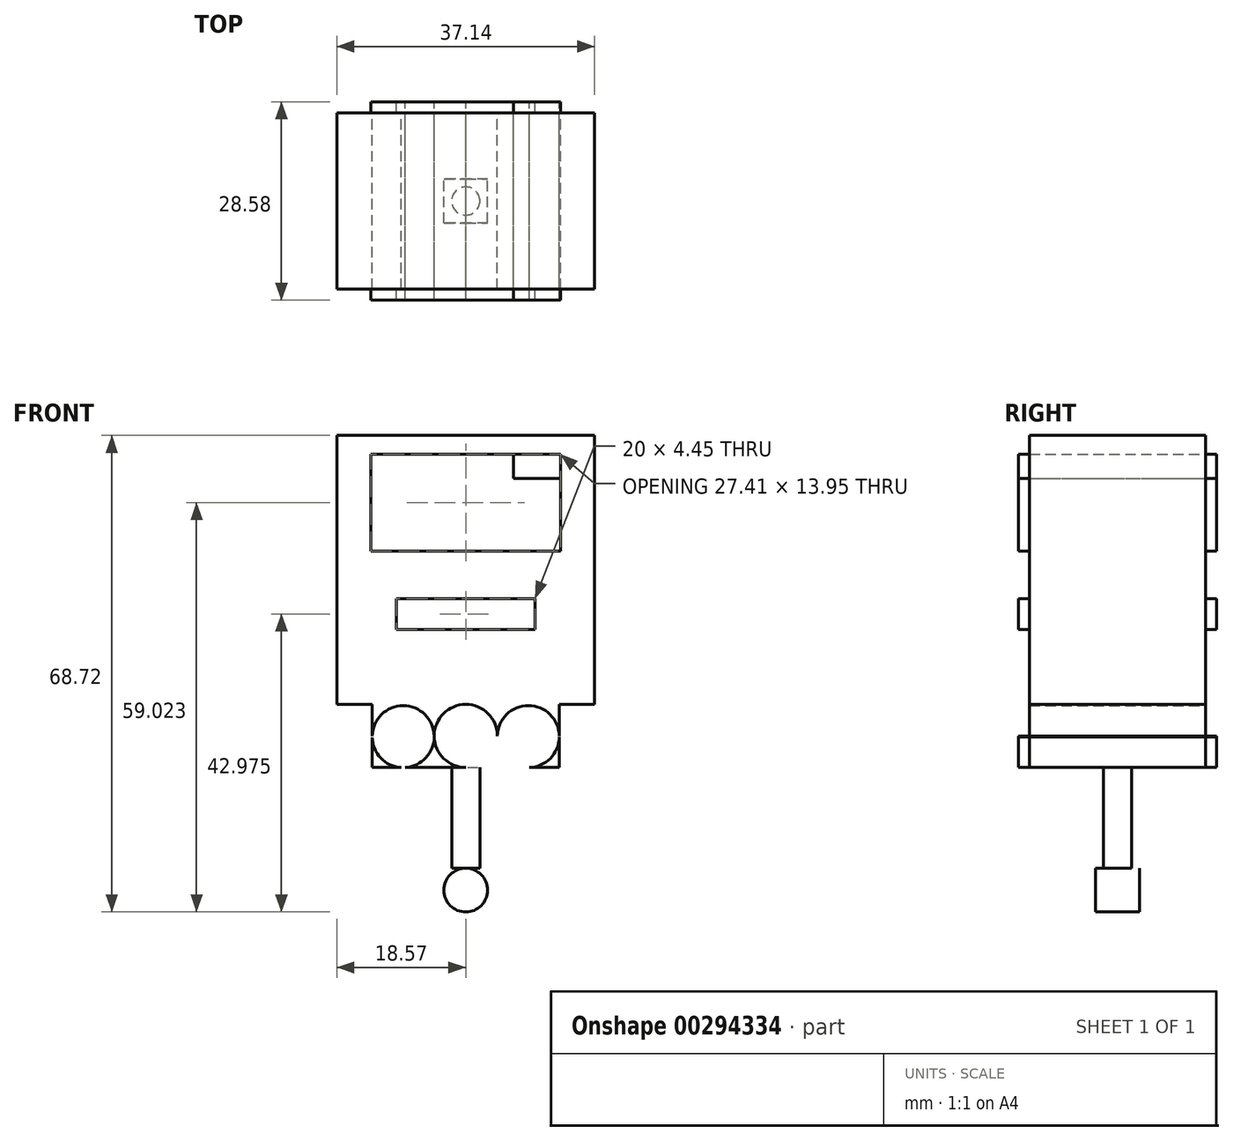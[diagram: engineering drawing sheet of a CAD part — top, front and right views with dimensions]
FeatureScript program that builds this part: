
annotation { "Feature Type Name" : "Feature", "Feature Type Description" : "" }
export const myFeature = defineFeature(function(context is Context, id is Id, definition is map)
    precondition{}
    {
        {
            var Q0;
            Q0=qCreatedBy(makeId("Front.planeOp"),FACE);
            var sketch = newSketch(context, id + "F0", { "sketchPlane" : qUnion([Q0])});
            skLineSegment(sketch, "E0.top", {"start": v(-13.49, -4.55) * mm, "end": v(13.49, -4.55) * mm});
            skLineSegment(sketch, "E0.left", {"start": v(-13.49, 4.55) * mm, "end": v(-13.49, -4.55) * mm});
            skLineSegment(sketch, "E0.right", {"start": v(13.49, 4.55) * mm, "end": v(13.49, -4.55) * mm});
            skPoint(sketch, "E0.middle", {"position": v(0, 0) * mm});
            skLineSegment(sketch, "E1", {"start": v(-13.49, 4.55) * mm, "end": v(-18.57, 4.55) * mm});
            skLineSegment(sketch, "E2", {"start": v(13.49, 4.55) * mm, "end": v(18.57, 4.55) * mm});
            skLineSegment(sketch, "E3.top", {"start": v(-18.57, 43.34) * mm, "end": v(18.57, 43.34) * mm});
            skLineSegment(sketch, "E3.left", {"start": v(-18.57, 4.55) * mm, "end": v(-18.57, 43.34) * mm});
            skLineSegment(sketch, "E3.right", {"start": v(18.57, 4.55) * mm, "end": v(18.57, 43.34) * mm});
            skPoint(sketch, "E4.endSnap0", {"position": v(0, -4.55) * mm});
            skLineSegment(sketch, "E5.bottom", {"start": v(-2.04, -4.55) * mm, "end": v(2.04, -4.55) * mm});
            skLineSegment(sketch, "E5.right", {"start": v(2.04, -4.55) * mm, "end": v(2.04, -19.08) * mm});
            skPoint(sketch, "E5.middle", {"position": v(0, -11.82) * mm});
            skCircle(sketch, "E6", {"center": v(0, 0) * mm, "radius": 4.55 * mm});
            skCircle(sketch, "E7", {"center": v(9.02, -0.09) * mm, "radius": 4.47 * mm});
            skPoint(sketch, "E7.second.point", {"position": v(4.55, 0) * mm});
            skPoint(sketch, "E7.third.point", {"position": v(8.9, -4.55) * mm});
            skCircle(sketch, "E8", {"center": v(-9.02, -0.1) * mm, "radius": 4.47 * mm});
            skPoint(sketch, "E8.second.point", {"position": v(-4.55, 0) * mm});
            skPoint(sketch, "E8.third.point", {"position": v(-8.7, -4.55) * mm});
            skLineSegment(sketch, "E9.bottom", {"start": v(-13.7, 26.67) * mm, "end": v(13.7, 26.67) * mm});
            skLineSegment(sketch, "E9.top", {"start": v(-13.7, 40.62) * mm, "end": v(13.7, 40.62) * mm});
            skLineSegment(sketch, "E9.left", {"start": v(-13.7, 26.67) * mm, "end": v(-13.7, 40.62) * mm});
            skLineSegment(sketch, "E9.right", {"start": v(13.7, 26.67) * mm, "end": v(13.7, 40.62) * mm});
            skPoint(sketch, "E9.middle", {"position": v(0, 33.64) * mm});
            skLineSegment(sketch, "E10.bottom", {"start": v(-10, 19.82) * mm, "end": v(10, 19.82) * mm});
            skLineSegment(sketch, "E10.top", {"start": v(-10, 15.37) * mm, "end": v(10, 15.37) * mm});
            skLineSegment(sketch, "E10.left", {"start": v(-10, 19.82) * mm, "end": v(-10, 15.37) * mm});
            skLineSegment(sketch, "E10.right", {"start": v(10, 19.82) * mm, "end": v(10, 15.37) * mm});
            skPoint(sketch, "E10.middle", {"position": v(0, 17.6) * mm});
            skLineSegment(sketch, "E11", {"start": v(0, 33.64) * mm, "end": v(0, 26.67) * mm});
            skLineSegment(sketch, "E12", {"start": v(0, 26.67) * mm, "end": v(0, 33.64) * mm});
            skLineSegment(sketch, "E13", {"start": v(0, 33.64) * mm, "end": v(0, 40.62) * mm});
            skLineSegment(sketch, "E14", {"start": v(0, 33.64) * mm, "end": v(13.7, 33.64) * mm});
            skLineSegment(sketch, "E15", {"start": v(13.7, 33.64) * mm, "end": v(-13.7, 33.64) * mm});
            skLineSegment(sketch, "E16", {"start": v(-13.7, 33.64) * mm, "end": v(-13.7, 26.67) * mm});
            skLineSegment(sketch, "E17", {"start": v(-13.7, 30.16) * mm, "end": v(13.7, 30.16) * mm});
            skLineSegment(sketch, "E18", {"start": v(13.7, 40.62) * mm, "end": v(13.7, 33.64) * mm});
            skLineSegment(sketch, "E19", {"start": v(13.7, 37.13) * mm, "end": v(-13.7, 37.13) * mm});
            skLineSegment(sketch, "E20", {"start": v(-13.7, 40.62) * mm, "end": v(0, 40.62) * mm});
            skLineSegment(sketch, "E21", {"start": v(-6.85, 40.62) * mm, "end": v(-6.85, 26.67) * mm});
            skLineSegment(sketch, "E22", {"start": v(0, 40.62) * mm, "end": v(13.7, 40.62) * mm});
            skLineSegment(sketch, "E23", {"start": v(6.85, 40.62) * mm, "end": v(6.85, 26.67) * mm});
            skLineSegment(sketch, "E24", {"start": v(0, 19.82) * mm, "end": v(0, 15.37) * mm});
            skLineSegment(sketch, "E25", {"start": v(-10, 19.82) * mm, "end": v(0, 19.82) * mm});
            skLineSegment(sketch, "E26", {"start": v(-5, 19.82) * mm, "end": v(-5, 15.37) * mm});
            skLineSegment(sketch, "E27", {"start": v(-5, 15.37) * mm, "end": v(10, 15.37) * mm});
            skLineSegment(sketch, "E28", {"start": v(0, 19.82) * mm, "end": v(10, 19.82) * mm});
            skLineSegment(sketch, "E29", {"start": v(5, 19.82) * mm, "end": v(5, 15.37) * mm});
            skCircle(sketch, "E30", {"center": v(0, -22.23) * mm, "radius": 3.15 * mm});
            skLineSegment(sketch, "E31", {"start": v(0, -36.46) * mm, "end": v(0, -30.92) * mm});
            skLineSegment(sketch, "E32", {"start": v(0, -30.92) * mm, "end": v(0, -43.93) * mm});
            skLineSegment(sketch, "E33", {"start": v(0, -19.08) * mm, "end": v(0, -4.55) * mm});
            skLineSegment(sketch, "E34", {"start": v(2.04, -19.08) * mm, "end": v(0, -19.08) * mm});
            skSolve(sketch);
        }
        {
            var Q0;
            {var subQ7=sQuery(id+"F0.wireOp",EDGE,"E1");Q0=makeQuery(id+"F0.imprint","IMPRINT",FACE,{"disambiguationData":[TD([[makeQuery(id+"F0.imprint","IMPRINT",EDGE,{"derivedFrom":subQ7}),-1.0]])]});}
            var Q1;
            {var subQ0=sQuery(id+"F0.wireOp",EDGE,"E0.left");var subQ1=sQuery(id+"F0.wireOp",EDGE,"E0.top");var subQ2=makeQuery(id+"F0.imprint","INTERSECT",VERTEX,{"derivedFrom":[subQ1,subQ0]});Q1=makeQuery(id+"F0.imprint","IMPRINT",FACE,{"disambiguationData":[TD([[makeQuery(id+"F0.imprint","IMPRINT",EDGE,{"disambiguationData":[TD([[subQ2,-1.0]])],"derivedFrom":subQ1}),1.0]])]});}
            var Q2;
            {var subQ3=sQuery(id+"F0.wireOp",EDGE,"E8");var subQ5=sQuery(id+"F0.wireOp",EDGE,"E6");var subQ7=makeQuery(id+"F0.imprint","INTERSECT",VERTEX,{"disambiguationData":[OD(1.0)],"derivedFrom":[subQ5,subQ3]});Q2=makeQuery(id+"F0.imprint","IMPRINT",FACE,{"disambiguationData":[TD([[makeQuery(id+"F0.imprint","IMPRINT",EDGE,{"disambiguationData":[TD([[subQ7,-1.0]])],"derivedFrom":subQ5}),-1.0]])]});}
            var Q3;
            {var subQ0=sQuery(id+"F0.wireOp",EDGE,"E5.bottom");var subQ5=sQuery(id+"F0.wireOp",EDGE,"E6");var subQ6=makeQuery(id+"F0.imprint","INTERSECT",VERTEX,{"derivedFrom":[subQ0,subQ5]});Q3=makeQuery(id+"F0.imprint","IMPRINT",FACE,{"disambiguationData":[TD([[makeQuery(id+"F0.imprint","IMPRINT",EDGE,{"disambiguationData":[TD([[subQ6,-1.0]])],"derivedFrom":subQ5}),-1.0]])]});}
            var Q4;
            {var subQ0=sQuery(id+"F0.wireOp",EDGE,"E0.right");var subQ1=sQuery(id+"F0.wireOp",EDGE,"E0.top");var subQ2=makeQuery(id+"F0.imprint","INTERSECT",VERTEX,{"derivedFrom":[subQ1,subQ0]});Q4=makeQuery(id+"F0.imprint","IMPRINT",FACE,{"disambiguationData":[TD([[makeQuery(id+"F0.imprint","IMPRINT",EDGE,{"disambiguationData":[TD([[subQ2,1.0]])],"derivedFrom":subQ1}),1.0]])]});}
            extrude(context, id + "F1", {"entities" : qUnion([Q0, Q1, Q2, Q3, Q4]), "endBound" : BoundingType.SYMMETRIC, "depth" : 25.4 * mm});
        }
        {
            var Q0;
            Q0=makeQuery(id+"F0.imprint","IMPRINT",FACE,{"disambiguationData":[TD([[makeQuery(id+"F0.imprint","IMPRINT",EDGE,{"derivedFrom":sQuery(id+"F0.wireOp",EDGE,"E10.top")}),1.0]])]});
            var Q1;
            {var subQ0=sQuery(id+"F0.wireOp",EDGE,"E24");Q1=makeQuery(id+"F0.imprint","IMPRINT",FACE,{"disambiguationData":[TD([[makeQuery(id+"F0.imprint","IMPRINT",EDGE,{"derivedFrom":subQ0}),-1.0]])]});}
            var Q2;
            {var subQ0=sQuery(id+"F0.wireOp",EDGE,"E24");Q2=makeQuery(id+"F0.imprint","IMPRINT",FACE,{"disambiguationData":[TD([[makeQuery(id+"F0.imprint","IMPRINT",EDGE,{"derivedFrom":subQ0}),1.0]])]});}
            var Q3;
            {var subQ0=sQuery(id+"F0.wireOp",EDGE,"E10.right");Q3=makeQuery(id+"F0.imprint","IMPRINT",FACE,{"disambiguationData":[TD([[makeQuery(id+"F0.imprint","IMPRINT",EDGE,{"derivedFrom":subQ0}),-1.0]])]});}
            extrude(context, id + "F2", {"entities" : qUnion([Q0, Q1, Q2, Q3]), "operationType" : NewBodyOperationType.ADD, "endBound" : BoundingType.SYMMETRIC, "depth" : 28.57 * mm});
        }
        {
            var Q0;
            {var subQ1=sQuery(id+"F0.wireOp",EDGE,"E9.left");var subQ3=sQuery(id+"F0.wireOp",EDGE,"E19");var subQ4=makeQuery(id+"F0.imprint","INTERSECT",VERTEX,{"derivedFrom":[subQ1,subQ3]});Q0=makeQuery(id+"F0.imprint","IMPRINT",FACE,{"disambiguationData":[TD([[makeQuery(id+"F0.imprint","IMPRINT",EDGE,{"disambiguationData":[TD([[subQ4,1.0]])],"derivedFrom":subQ3}),1.0]])]});}
            var Q1;
            {var subQ0=sQuery(id+"F0.wireOp",EDGE,"E20");var subQ1=sQuery(id+"F0.wireOp",EDGE,"E9.left");var subQ2=makeQuery(id+"F0.imprint","INTERSECT",VERTEX,{"derivedFrom":[subQ1,subQ0]});Q1=makeQuery(id+"F0.imprint","IMPRINT",FACE,{"disambiguationData":[TD([[makeQuery(id+"F0.imprint","IMPRINT",EDGE,{"disambiguationData":[TD([[subQ2,1.0]])],"derivedFrom":subQ1}),-1.0]])]});}
            var Q2;
            {var subQ1=sQuery(id+"F0.wireOp",EDGE,"E13");var subQ3=sQuery(id+"F0.wireOp",EDGE,"E19");var subQ4=makeQuery(id+"F0.imprint","INTERSECT",VERTEX,{"derivedFrom":[subQ1,subQ3]});Q2=makeQuery(id+"F0.imprint","IMPRINT",FACE,{"disambiguationData":[TD([[makeQuery(id+"F0.imprint","IMPRINT",EDGE,{"disambiguationData":[TD([[subQ4,-1.0]])],"derivedFrom":subQ3}),-1.0]])]});}
            var Q3;
            {var subQ1=sQuery(id+"F0.wireOp",EDGE,"E13");var subQ3=sQuery(id+"F0.wireOp",EDGE,"E19");var subQ4=makeQuery(id+"F0.imprint","INTERSECT",VERTEX,{"derivedFrom":[subQ1,subQ3]});Q3=makeQuery(id+"F0.imprint","IMPRINT",FACE,{"disambiguationData":[TD([[makeQuery(id+"F0.imprint","IMPRINT",EDGE,{"disambiguationData":[TD([[subQ4,1.0]])],"derivedFrom":subQ3}),-1.0]])]});}
            var Q4;
            {var subQ1=sQuery(id+"F0.wireOp",EDGE,"E12");var subQ3=sQuery(id+"F0.wireOp",EDGE,"E17");var subQ4=makeQuery(id+"F0.imprint","INTERSECT",VERTEX,{"derivedFrom":[subQ1,subQ3]});Q4=makeQuery(id+"F0.imprint","IMPRINT",FACE,{"disambiguationData":[TD([[makeQuery(id+"F0.imprint","IMPRINT",EDGE,{"disambiguationData":[TD([[subQ4,1.0]])],"derivedFrom":subQ3}),1.0]])]});}
            var Q5;
            {var subQ0=sQuery(id+"F0.wireOp",EDGE,"E22");var subQ1=sQuery(id+"F0.wireOp",EDGE,"E18");var subQ2=makeQuery(id+"F0.imprint","INTERSECT",VERTEX,{"derivedFrom":[subQ1,subQ0]});Q5=makeQuery(id+"F0.imprint","IMPRINT",FACE,{"disambiguationData":[TD([[makeQuery(id+"F0.imprint","IMPRINT",EDGE,{"disambiguationData":[TD([[subQ2,-1.0]])],"derivedFrom":subQ1}),-1.0]])]});}
            var Q6;
            {var subQ0=sQuery(id+"F0.wireOp",EDGE,"E18");var subQ5=sQuery(id+"F0.wireOp",EDGE,"E19");var subQ7=makeQuery(id+"F0.imprint","INTERSECT",VERTEX,{"derivedFrom":[subQ0,subQ5]});Q6=makeQuery(id+"F0.imprint","IMPRINT",FACE,{"disambiguationData":[TD([[makeQuery(id+"F0.imprint","IMPRINT",EDGE,{"disambiguationData":[TD([[subQ7,-1.0]])],"derivedFrom":subQ5}),1.0]])]});}
            var Q7;
            {var subQ1=sQuery(id+"F0.wireOp",EDGE,"E13");var subQ3=sQuery(id+"F0.wireOp",EDGE,"E19");var subQ4=makeQuery(id+"F0.imprint","INTERSECT",VERTEX,{"derivedFrom":[subQ1,subQ3]});Q7=makeQuery(id+"F0.imprint","IMPRINT",FACE,{"disambiguationData":[TD([[makeQuery(id+"F0.imprint","IMPRINT",EDGE,{"disambiguationData":[TD([[subQ4,1.0]])],"derivedFrom":subQ3}),1.0]])]});}
            var Q8;
            {var subQ1=sQuery(id+"F0.wireOp",EDGE,"E13");var subQ3=sQuery(id+"F0.wireOp",EDGE,"E19");var subQ4=makeQuery(id+"F0.imprint","INTERSECT",VERTEX,{"derivedFrom":[subQ1,subQ3]});Q8=makeQuery(id+"F0.imprint","IMPRINT",FACE,{"disambiguationData":[TD([[makeQuery(id+"F0.imprint","IMPRINT",EDGE,{"disambiguationData":[TD([[subQ4,-1.0]])],"derivedFrom":subQ3}),1.0]])]});}
            var Q9;
            {var subQ1=sQuery(id+"F0.wireOp",EDGE,"E9.right");var subQ3=sQuery(id+"F0.wireOp",EDGE,"E17");var subQ4=makeQuery(id+"F0.imprint","INTERSECT",VERTEX,{"derivedFrom":[subQ1,subQ3]});Q9=makeQuery(id+"F0.imprint","IMPRINT",FACE,{"disambiguationData":[TD([[makeQuery(id+"F0.imprint","IMPRINT",EDGE,{"disambiguationData":[TD([[subQ4,1.0]])],"derivedFrom":subQ3}),1.0]])]});}
            var Q10;
            {var subQ0=sQuery(id+"F0.wireOp",EDGE,"E9.right");var subQ1=sQuery(id+"F0.wireOp",EDGE,"E9.bottom");var subQ2=makeQuery(id+"F0.imprint","INTERSECT",VERTEX,{"derivedFrom":[subQ1,subQ0]});Q10=makeQuery(id+"F0.imprint","IMPRINT",FACE,{"disambiguationData":[TD([[makeQuery(id+"F0.imprint","IMPRINT",EDGE,{"disambiguationData":[TD([[subQ2,1.0]])],"derivedFrom":subQ1}),1.0]])]});}
            var Q11;
            {var subQ0=sQuery(id+"F0.wireOp",EDGE,"E12");var subQ1=sQuery(id+"F0.wireOp",EDGE,"E9.bottom");var subQ2=makeQuery(id+"F0.imprint","INTERSECT",VERTEX,{"derivedFrom":[subQ1,subQ0]});Q11=makeQuery(id+"F0.imprint","IMPRINT",FACE,{"disambiguationData":[TD([[makeQuery(id+"F0.imprint","IMPRINT",EDGE,{"disambiguationData":[TD([[subQ2,-1.0]])],"derivedFrom":subQ1}),1.0]])]});}
            var Q12;
            {var subQ1=sQuery(id+"F0.wireOp",EDGE,"E12");var subQ3=sQuery(id+"F0.wireOp",EDGE,"E17");var subQ4=makeQuery(id+"F0.imprint","INTERSECT",VERTEX,{"derivedFrom":[subQ1,subQ3]});Q12=makeQuery(id+"F0.imprint","IMPRINT",FACE,{"disambiguationData":[TD([[makeQuery(id+"F0.imprint","IMPRINT",EDGE,{"disambiguationData":[TD([[subQ4,-1.0]])],"derivedFrom":subQ3}),1.0]])]});}
            var Q13;
            {var subQ0=sQuery(id+"F0.wireOp",EDGE,"E12");var subQ1=sQuery(id+"F0.wireOp",EDGE,"E9.bottom");var subQ2=makeQuery(id+"F0.imprint","INTERSECT",VERTEX,{"derivedFrom":[subQ1,subQ0]});Q13=makeQuery(id+"F0.imprint","IMPRINT",FACE,{"disambiguationData":[TD([[makeQuery(id+"F0.imprint","IMPRINT",EDGE,{"disambiguationData":[TD([[subQ2,1.0]])],"derivedFrom":subQ1}),1.0]])]});}
            var Q14;
            {var subQ0=sQuery(id+"F0.wireOp",EDGE,"E16");var subQ1=sQuery(id+"F0.wireOp",EDGE,"E9.bottom");var subQ2=makeQuery(id+"F0.imprint","INTERSECT",VERTEX,{"derivedFrom":[subQ1,subQ0]});Q14=makeQuery(id+"F0.imprint","IMPRINT",FACE,{"disambiguationData":[TD([[makeQuery(id+"F0.imprint","IMPRINT",EDGE,{"disambiguationData":[TD([[subQ2,-1.0]])],"derivedFrom":subQ1}),1.0]])]});}
            var Q15;
            {var subQ0=sQuery(id+"F0.wireOp",EDGE,"E16");var subQ5=sQuery(id+"F0.wireOp",EDGE,"E17");var subQ6=makeQuery(id+"F0.imprint","INTERSECT",VERTEX,{"derivedFrom":[subQ0,subQ5]});Q15=makeQuery(id+"F0.imprint","IMPRINT",FACE,{"disambiguationData":[TD([[makeQuery(id+"F0.imprint","IMPRINT",EDGE,{"disambiguationData":[TD([[subQ6,-1.0]])],"derivedFrom":subQ5}),1.0]])]});}
            extrude(context, id + "F3", {"entities" : qUnion([Q0, Q1, Q2, Q3, Q4, Q5, Q6, Q7, Q8, Q9, Q10, Q11, Q12, Q13, Q14, Q15]), "operationType" : NewBodyOperationType.ADD, "endBound" : BoundingType.SYMMETRIC, "depth" : 28.57 * mm});
        }
        {
            var Q0;
            {var subQ0=sQuery(id+"F0.wireOp",EDGE,"E7");var subQ7=sQuery(id+"F0.wireOp",EDGE,"E0.top");var subQ8=makeQuery(id+"F0.imprint","INTERSECT",VERTEX,{"disambiguationData":[OD(0.0)],"derivedFrom":[subQ7,subQ0]});Q0=makeQuery(id+"F0.imprint","IMPRINT",FACE,{"disambiguationData":[TD([[makeQuery(id+"F0.imprint","IMPRINT",EDGE,{"disambiguationData":[TD([[subQ8,-1.0]])],"derivedFrom":subQ7}),1.0]])]});}
            extrude(context, id + "F4", {"entities" : qUnion([Q0]), "endBound" : BoundingType.SYMMETRIC, "depth" : 28.57 * mm});
        }
        {
            var Q0;
            {var subQ1=sQuery(id+"F0.wireOp",EDGE,"E6");var subQ4=sQuery(id+"F0.wireOp",EDGE,"E8");var subQ6=makeQuery(id+"F0.imprint","INTERSECT",VERTEX,{"disambiguationData":[OD(2.0)],"derivedFrom":[subQ1,subQ4]});Q0=makeQuery(id+"F0.imprint","IMPRINT",FACE,{"disambiguationData":[TD([[makeQuery(id+"F0.imprint","IMPRINT",EDGE,{"disambiguationData":[TD([[subQ6,1.0]])],"derivedFrom":subQ1}),1.0]])]});}
            extrude(context, id + "F5", {"entities" : qUnion([Q0]), "endBound" : BoundingType.SYMMETRIC, "depth" : 28.57 * mm});
        }
        {
            var Q0;
            {var subQ0=sQuery(id+"F0.wireOp",EDGE,"E8");var subQ7=sQuery(id+"F0.wireOp",EDGE,"E0.top");var subQ8=makeQuery(id+"F0.imprint","INTERSECT",VERTEX,{"disambiguationData":[OD(0.0)],"derivedFrom":[subQ7,subQ0]});Q0=makeQuery(id+"F0.imprint","IMPRINT",FACE,{"disambiguationData":[TD([[makeQuery(id+"F0.imprint","IMPRINT",EDGE,{"disambiguationData":[TD([[subQ8,-1.0]])],"derivedFrom":subQ7}),1.0]])]});}
            extrude(context, id + "F6", {"entities" : qUnion([Q0]), "endBound" : BoundingType.SYMMETRIC, "depth" : 28.57 * mm});
        }
        {
            var Q0;
            {var subQ0=sQuery(id+"F0.wireOp",EDGE,"E5.right");Q0=makeQuery(id+"F0.imprint","IMPRINT",FACE,{"disambiguationData":[TD([[makeQuery(id+"F0.imprint","IMPRINT",EDGE,{"derivedFrom":subQ0}),-1.0]])]});}
            var Q1;
            Q1=sQuery(id+"F0.wireOp",EDGE,"E31");
            revolve(context, id + "F7", {"entities" : qUnion([Q0]), "axis" : qUnion([Q1]), "revolveType" : RevolveType.FULL});
        }
        {
            var Q0;
            Q0=makeQuery(id+"F0.imprint","IMPRINT",FACE,{"disambiguationData":[TD([[makeQuery(id+"F0.imprint","IMPRINT",EDGE,{"derivedFrom":sQuery(id+"F0.wireOp",EDGE,"E30")}),1.0]])]});
            extrude(context, id + "F8", {"entities" : qUnion([Q0]), "operationType" : NewBodyOperationType.ADD, "endBound" : BoundingType.SYMMETRIC, "depth" : 6.35 * mm});
        }
    });
